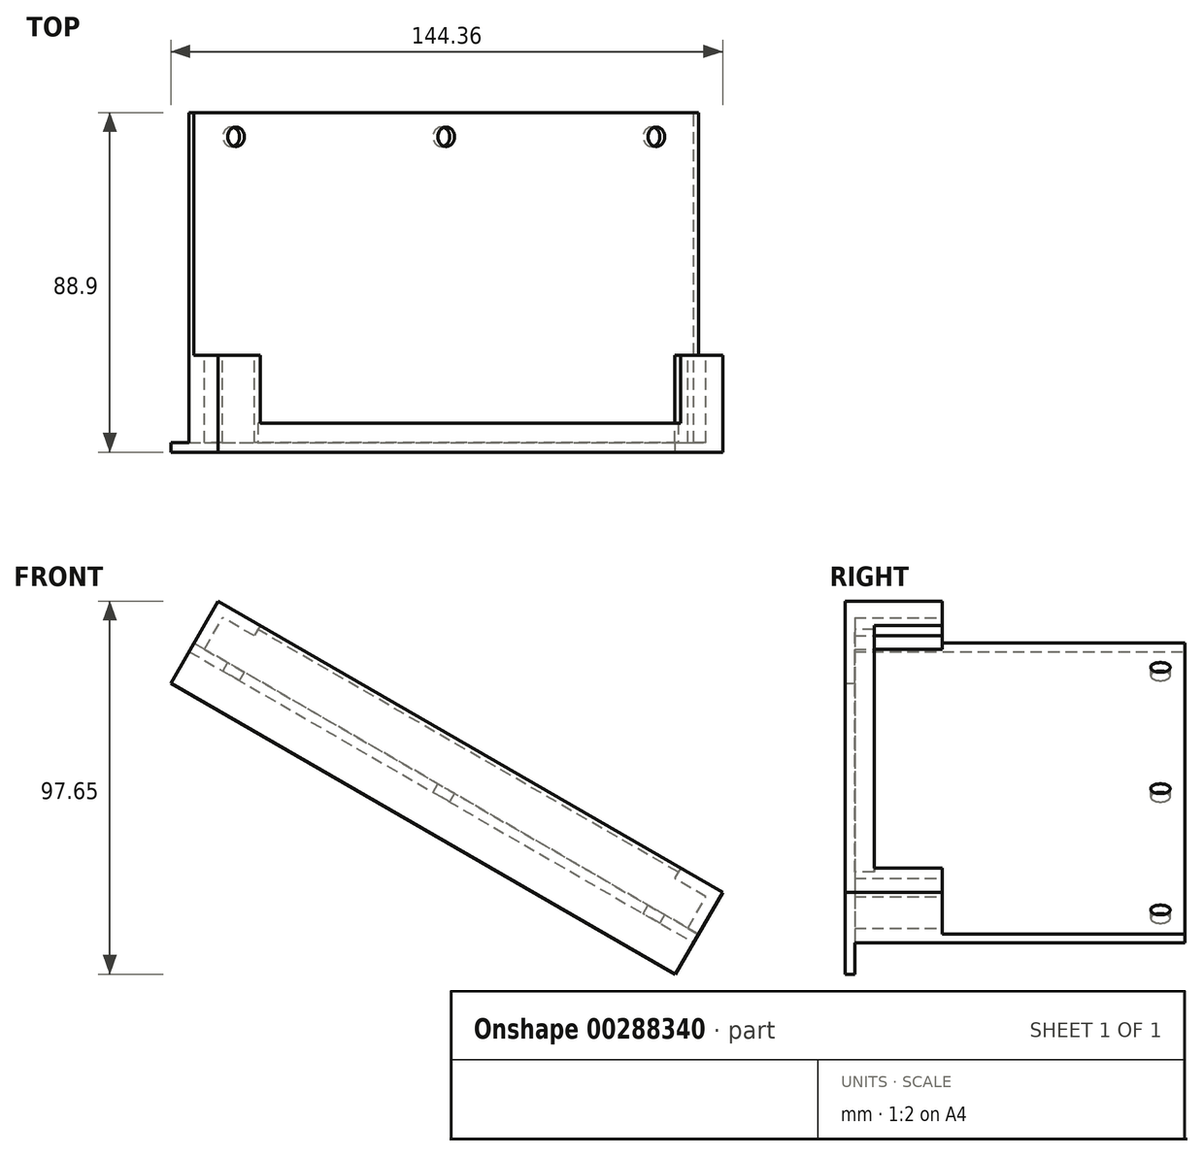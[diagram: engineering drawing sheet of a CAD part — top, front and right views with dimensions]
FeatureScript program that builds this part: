
annotation { "Feature Type Name" : "Feature", "Feature Type Description" : "" }
export const myFeature = defineFeature(function(context is Context, id is Id, definition is map)
    precondition{}
    {
        {
            var Q0;
            Q0=qCreatedBy(makeId("Top.planeOp"),FACE);
            var sketch = newSketch(context, id + "F0", { "sketchPlane" : qUnion([Q0])});
            skLineSegment(sketch, "E0.bottom", {"start": v(76.2, -44.45) * mm, "end": v(-76.2, -44.45) * mm});
            skLineSegment(sketch, "E0.top", {"start": v(76.2, 44.45) * mm, "end": v(-76.2, 44.45) * mm});
            skLineSegment(sketch, "E0.left", {"start": v(76.2, -44.45) * mm, "end": v(76.2, 44.45) * mm});
            skLineSegment(sketch, "E0.right", {"start": v(-76.2, -44.45) * mm, "end": v(-76.2, 44.45) * mm});
            skPoint(sketch, "E0.middle", {"position": v(0, 0) * mm});
            skSolve(sketch);
        }
        {
            var Q0;
            Q0 = qSketchRegion(id + "F0", true);
            extrude(context, id + "F1", {"entities" : qUnion([Q0]), "depth" : 2.54 * mm});
        }
        {
            var Q0;
            Q0=makeQuery(id+"F1.opExtrude","CAP_FACE",FACE,{"disambiguationData":[OSD([sQuery(id+"F0.wireOp",EDGE,"E0.bottom"),sQuery(id+"F0.wireOp",EDGE,"E0.top"),sQuery(id+"F0.wireOp",EDGE,"E0.left"),sQuery(id+"F0.wireOp",EDGE,"E0.right")])],"isStart":false});
            var sketch = newSketch(context, id + "F2", { "sketchPlane" : qUnion([Q0])});
            skLineSegment(sketch, "E1.bottom", {"start": v(-63.5, -41.91) * mm, "end": v(63.5, -41.91) * mm});
            skLineSegment(sketch, "E1.top", {"start": v(-76.2, -44.45) * mm, "end": v(76.2, -44.45) * mm});
            skLineSegment(sketch, "E2", {"start": v(-76.2, -44.45) * mm, "end": v(-76.2, -19.05) * mm});
            skLineSegment(sketch, "E3", {"start": v(-76.2, -19.05) * mm, "end": v(-63.5, -19.05) * mm});
            skLineSegment(sketch, "E4", {"start": v(63.5, -19.05) * mm, "end": v(76.2, -19.05) * mm});
            skLineSegment(sketch, "E5", {"start": v(-63.5, -19.05) * mm, "end": v(-63.5, -41.91) * mm});
            skLineSegment(sketch, "E6", {"start": v(63.5, -19.05) * mm, "end": v(63.5, -41.91) * mm});
            skLineSegment(sketch, "E7", {"start": v(76.2, -19.05) * mm, "end": v(76.2, -44.45) * mm});
            skSolve(sketch);
        }
        {
            var Q0;
            Q0 = qSketchRegion(id + "F2", true);
            extrude(context, id + "F3", {"entities" : qUnion([Q0]), "operationType" : NewBodyOperationType.ADD, "depth" : 12.7 * mm});
        }
        {
            var Q0;
            Q0=makeQuery(id+"F3.opExtrude","SWEPT_FACE",FACE,{"disambiguationData":[OSD([sQuery(id+"F2.wireOp",EDGE,"E1.bottom")])]});
            var sketch = newSketch(context, id + "F4", { "sketchPlane" : qUnion([Q0])});
            skLineSegment(sketch, "E8.bottom", {"start": v(-63.5, 15.24) * mm, "end": v(63.5, 15.24) * mm});
            skLineSegment(sketch, "E8.top", {"start": v(-63.5, 13.97) * mm, "end": v(63.5, 13.97) * mm});
            skLineSegment(sketch, "E8.left", {"start": v(-63.5, 15.24) * mm, "end": v(-63.5, 13.97) * mm});
            skLineSegment(sketch, "E8.right", {"start": v(63.5, 15.24) * mm, "end": v(63.5, 13.97) * mm});
            skSolve(sketch);
        }
        {
            var Q0;
            Q0 = qSketchRegion(id + "F4", true);
            extrude(context, id + "F5", {"entities" : qUnion([Q0]), "operationType" : NewBodyOperationType.ADD, "depth" : 5.08 * mm});
        }
        {
            var Q0;
            Q0=makeQuery(id+"F3.opExtrude","SWEPT_FACE",FACE,{"disambiguationData":[OSD([sQuery(id+"F2.wireOp",EDGE,"E4")])]});
            var sketch = newSketch(context, id + "F6", { "sketchPlane" : qUnion([Q0])});
            skLineSegment(sketch, "E9.bottom", {"start": v(-73.03, 2.54) * mm, "end": v(73.03, 2.54) * mm});
            skLineSegment(sketch, "E9.top", {"start": v(-73.02, 12.06) * mm, "end": v(73.02, 12.06) * mm});
            skLineSegment(sketch, "E9.left", {"start": v(-73.03, 2.54) * mm, "end": v(-73.03, 12.06) * mm});
            skLineSegment(sketch, "E9.right", {"start": v(73.02, 2.54) * mm, "end": v(73.02, 12.07) * mm});
            skPoint(sketch, "E10", {"position": v(0, 2.54) * mm});
            skSolve(sketch);
        }
        {
            var Q0;
            Q0 = qSketchRegion(id + "F6", true);
            var Q1;
            Q1=makeQuery(id+"F3.opExtrude","SWEPT_FACE",FACE,{"disambiguationData":[OSD([sQuery(id+"F2.wireOp",EDGE,"E1.bottom")])]});
            extrude(context, id + "F7", {"entities" : qUnion([Q0]), "operationType" : NewBodyOperationType.REMOVE, "endBound" : BoundingType.UP_TO_SURFACE, "oppositeDirection" : true, "endBoundEntityFace" : qUnion([Q1]), "depth" : 25.4 * mm});
        }
        {
            var Q0;
            Q0=makeQuery(id+"F7.boolean.opBoolean","MERGE",FACE,{"derivedFrom":[makeQuery(id+"F1.opExtrude","CAP_FACE",FACE,{"disambiguationData":[OSD([sQuery(id+"F0.wireOp",EDGE,"E0.bottom"),sQuery(id+"F0.wireOp",EDGE,"E0.top"),sQuery(id+"F0.wireOp",EDGE,"E0.left"),sQuery(id+"F0.wireOp",EDGE,"E0.right")])],"isStart":false}),makeQuery(id+"F7.opExtrude","SWEPT_FACE",FACE,{"disambiguationData":[OSD([sQuery(id+"F6.wireOp",EDGE,"CmoMC5kJ-x9Ux-V3P9-Jdot-7MtKv6RrJ7Bm.top")])]})]});
            var sketch = newSketch(context, id + "F8", { "sketchPlane" : qUnion([Q0])});
            skCircle(sketch, "E11", {"center": v(0, 38.1) * mm, "radius": 2.54 * mm});
            skCircle(sketch, "E12", {"center": v(-63.5, 38.1) * mm, "radius": 2.54 * mm});
            skCircle(sketch, "E13", {"center": v(63.5, 38.1) * mm, "radius": 2.54 * mm});
            skSolve(sketch);
        }
        {
            var Q0;
            Q0 = qSketchRegion(id + "F8", true);
            extrude(context, id + "F9", {"entities" : qUnion([Q0]), "operationType" : NewBodyOperationType.REMOVE, "endBound" : BoundingType.THROUGH_ALL, "oppositeDirection" : true, "depth" : 25.4 * mm});
        }
        {
            var Q0;
            Q0=makeQuery(id+"F1.opExtrude","CAP_FACE",FACE,{"disambiguationData":[OSD([sQuery(id+"F0.wireOp",EDGE,"E0.bottom"),sQuery(id+"F0.wireOp",EDGE,"E0.top"),sQuery(id+"F0.wireOp",EDGE,"E0.left"),sQuery(id+"F0.wireOp",EDGE,"E0.right")])],"isStart":true});
            var sketch = newSketch(context, id + "F10", { "sketchPlane" : qUnion([Q0])});
            skLineSegment(sketch, "E14.bottom", {"start": v(-76.2, 44.45) * mm, "end": v(76.2, 44.45) * mm});
            skLineSegment(sketch, "E14.top", {"start": v(-76.2, 41.91) * mm, "end": v(76.2, 41.91) * mm});
            skLineSegment(sketch, "E14.left", {"start": v(-76.2, 44.45) * mm, "end": v(-76.2, 41.91) * mm});
            skLineSegment(sketch, "E14.right", {"start": v(76.2, 44.45) * mm, "end": v(76.2, 41.91) * mm});
            skSolve(sketch);
        }
        {
            var Q0;
            Q0 = qSketchRegion(id + "F10", true);
            extrude(context, id + "F11", {"entities" : qUnion([Q0]), "operationType" : NewBodyOperationType.ADD, "depth" : 9.52 * mm});
        }
        {
            var Q0;
            Q0=makeQuery(id+"F1.opExtrude","SWEPT_BODY",BODY,{"disambiguationData":[OSD([sQuery(id+"F0.wireOp",EDGE,"E0.bottom"),sQuery(id+"F0.wireOp",EDGE,"E0.top"),sQuery(id+"F0.wireOp",EDGE,"E0.left"),sQuery(id+"F0.wireOp",EDGE,"E0.right")])]});
            var Q1;
            Q1=makeQuery(id+"F1.opExtrude","CAP_EDGE",EDGE,{"disambiguationData":[OSD([sQuery(id+"F0.wireOp",EDGE,"E0.right")])],"isStart":false});
            transform(context, id + "F12", {"entities" : qUnion([Q0]), "transformType" : TransformType.ROTATION, "transformAxis" : qUnion([Q1]), "angle" : 30 * degree, "makeCopy" : false});
        }
    });
